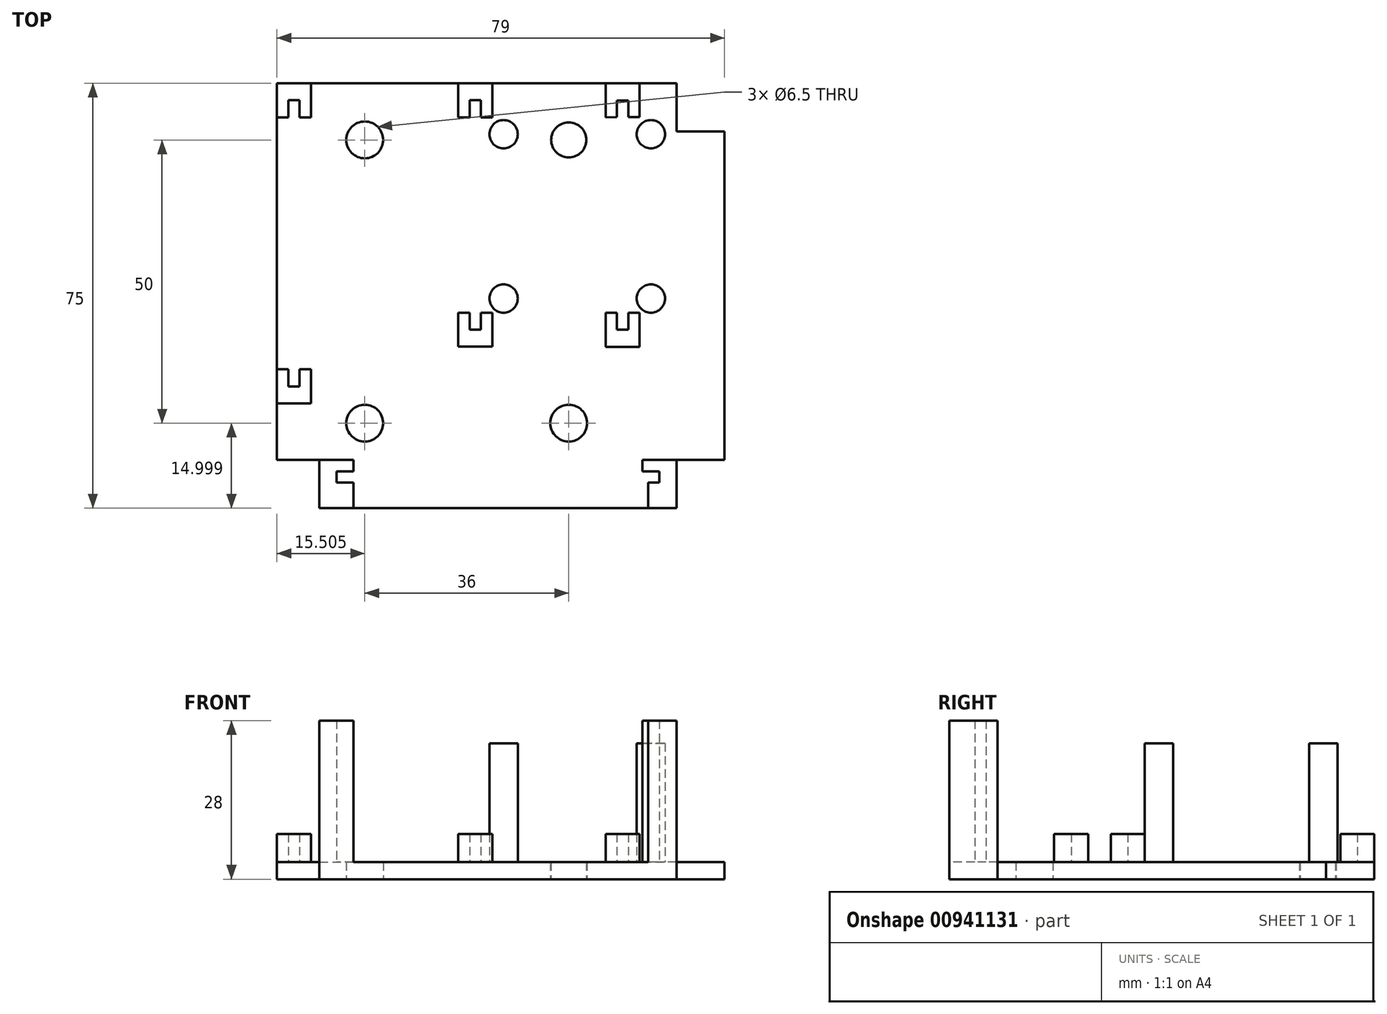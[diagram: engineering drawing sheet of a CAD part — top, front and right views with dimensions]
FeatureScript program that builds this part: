
annotation { "Feature Type Name" : "Feature", "Feature Type Description" : "" }
export const myFeature = defineFeature(function(context is Context, id is Id, definition is map)
    precondition{}
    {
        {
            var Q0;
            Q0=qCreatedBy(makeId("Top.planeOp"),FACE);
            var sketch = newSketch(context, id + "F0", { "sketchPlane" : qUnion([Q0])});
            skLineSegment(sketch, "E0", {"start": v(0, 50.14) * mm, "end": v(-25.4, 50.14) * mm});
            skLineSegment(sketch, "E1", {"start": v(-25.4, 50.14) * mm, "end": v(-25.4, -16.36) * mm});
            skLineSegment(sketch, "E2", {"start": v(-25.4, -16.36) * mm, "end": v(-17.9, -16.36) * mm});
            skLineSegment(sketch, "E3", {"start": v(-17.9, -16.36) * mm, "end": v(-17.9, -24.86) * mm});
            skLineSegment(sketch, "E4", {"start": v(-17.9, -24.86) * mm, "end": v(0, -24.86) * mm});
            skLineSegment(sketch, "E5", {"start": v(0, -24.86) * mm, "end": v(45.1, -24.86) * mm});
            skLineSegment(sketch, "E6", {"start": v(45.1, -24.86) * mm, "end": v(45.1, -16.36) * mm});
            skLineSegment(sketch, "E7", {"start": v(45.1, -16.36) * mm, "end": v(53.6, -16.36) * mm});
            skLineSegment(sketch, "E8", {"start": v(53.6, -16.36) * mm, "end": v(53.6, 41.64) * mm});
            skLineSegment(sketch, "E9", {"start": v(53.6, 41.64) * mm, "end": v(45.1, 41.64) * mm});
            skLineSegment(sketch, "E10", {"start": v(45.1, 41.64) * mm, "end": v(45.1, 50.14) * mm});
            skLineSegment(sketch, "E11", {"start": v(45.1, 50.14) * mm, "end": v(0, 50.14) * mm});
            skCircle(sketch, "E12", {"center": v(-9.9, 40.14) * mm, "radius": 3.25 * mm});
            skCircle(sketch, "E13", {"center": v(-9.9, -9.86) * mm, "radius": 3.25 * mm});
            skCircle(sketch, "E14", {"center": v(26.1, -9.86) * mm, "radius": 3.25 * mm});
            skCircle(sketch, "E15", {"center": v(26.1, 40.14) * mm, "radius": 3.1 * mm});
            skSolve(sketch);
        }
        {
            var Q0;
            Q0=makeQuery(id+"F0.imprint","IMPRINT",FACE,{"disambiguationData":[TD([[makeQuery(id+"F0.imprint","IMPRINT",EDGE,{"derivedFrom":sQuery(id+"F0.wireOp",EDGE,"E0")}),1.0]])]});
            extrude(context, id + "F1", {"entities" : qUnion([Q0]), "depth" : 3 * mm, "offsetDistance" : 25 * mm});
        }
        {
            var Q0;
            Q0=makeQuery(id+"F1.opExtrude","CAP_FACE",FACE,{"disambiguationData":[OSD([sQuery(id+"F0.wireOp",EDGE,"E0"),sQuery(id+"F0.wireOp",EDGE,"E1"),sQuery(id+"F0.wireOp",EDGE,"E2"),sQuery(id+"F0.wireOp",EDGE,"E3"),sQuery(id+"F0.wireOp",EDGE,"E4"),sQuery(id+"F0.wireOp",EDGE,"E5"),sQuery(id+"F0.wireOp",EDGE,"E6"),sQuery(id+"F0.wireOp",EDGE,"E7"),sQuery(id+"F0.wireOp",EDGE,"E8"),sQuery(id+"F0.wireOp",EDGE,"E9"),sQuery(id+"F0.wireOp",EDGE,"E10"),sQuery(id+"F0.wireOp",EDGE,"E11"),sQuery(id+"F0.wireOp",EDGE,"E12"),sQuery(id+"F0.wireOp",EDGE,"E13"),sQuery(id+"F0.wireOp",EDGE,"E14"),sQuery(id+"F0.wireOp",EDGE,"E15")])],"isStart":false});
            var sketch = newSketch(context, id + "F2", { "sketchPlane" : qUnion([Q0])});
            skLineSegment(sketch, "E16.bottom", {"start": v(-23.4, 47.14) * mm, "end": v(-21.4, 47.14) * mm});
            skLineSegment(sketch, "E16.top", {"start": v(-23.4, -3.36) * mm, "end": v(-21.4, -3.36) * mm});
            skLineSegment(sketch, "E16.left", {"start": v(-23.4, 47.14) * mm, "end": v(-23.4, -3.36) * mm});
            skLineSegment(sketch, "E16.right", {"start": v(-21.4, 47.14) * mm, "end": v(-21.4, -3.36) * mm});
            skLineSegment(sketch, "E17", {"start": v(-23.4, 44.14) * mm, "end": v(-25.4, 44.14) * mm});
            skLineSegment(sketch, "E18", {"start": v(-25.4, 44.14) * mm, "end": v(-25.4, 50.14) * mm});
            skLineSegment(sketch, "E19", {"start": v(-25.4, 50.14) * mm, "end": v(-19.4, 50.14) * mm});
            skLineSegment(sketch, "E20", {"start": v(-19.4, 50.14) * mm, "end": v(-19.4, 44.14) * mm});
            skLineSegment(sketch, "E21", {"start": v(-19.4, 44.14) * mm, "end": v(-21.4, 44.14) * mm});
            skLineSegment(sketch, "E22", {"start": v(-21.4, 44.14) * mm, "end": v(-21.4, 0) * mm});
            skLineSegment(sketch, "E23", {"start": v(-25.4, -0.36) * mm, "end": v(-25.4, -6.36) * mm});
            skLineSegment(sketch, "E24", {"start": v(-25.4, -6.36) * mm, "end": v(-19.4, -6.36) * mm});
            skLineSegment(sketch, "E25", {"start": v(-19.4, -6.36) * mm, "end": v(-19.4, -0.36) * mm});
            skLineSegment(sketch, "E26", {"start": v(-25.4, -0.36) * mm, "end": v(-23.4, -0.36) * mm});
            skLineSegment(sketch, "E27", {"start": v(-19.4, -0.36) * mm, "end": v(-21.4, -0.36) * mm});
            skLineSegment(sketch, "E28", {"start": v(6.6, 50.14) * mm, "end": v(6.6, 44.14) * mm});
            skLineSegment(sketch, "E29", {"start": v(6.6, 44.14) * mm, "end": v(8.6, 44.13) * mm});
            skLineSegment(sketch, "E30", {"start": v(8.6, 44.13) * mm, "end": v(8.6, 47.14) * mm});
            skLineSegment(sketch, "E31", {"start": v(8.6, 47.14) * mm, "end": v(10.6, 47.14) * mm});
            skLineSegment(sketch, "E32", {"start": v(10.6, 47.14) * mm, "end": v(10.6, 44.13) * mm});
            skLineSegment(sketch, "E33", {"start": v(10.6, 44.13) * mm, "end": v(12.6, 44.13) * mm});
            skLineSegment(sketch, "E34", {"start": v(12.6, 44.13) * mm, "end": v(12.6, 50.14) * mm});
            skLineSegment(sketch, "E35.top", {"start": v(8.6, 6.64) * mm, "end": v(10.6, 6.64) * mm});
            skLineSegment(sketch, "E35.left", {"start": v(8.6, 47.14) * mm, "end": v(8.6, 6.64) * mm});
            skLineSegment(sketch, "E35.right", {"start": v(10.6, 47.14) * mm, "end": v(10.6, 6.64) * mm});
            skLineSegment(sketch, "E36", {"start": v(8.6, 9.64) * mm, "end": v(6.6, 9.64) * mm});
            skLineSegment(sketch, "E37", {"start": v(6.6, 9.64) * mm, "end": v(6.6, 3.64) * mm});
            skLineSegment(sketch, "E38", {"start": v(6.6, 3.64) * mm, "end": v(12.6, 3.64) * mm});
            skLineSegment(sketch, "E39", {"start": v(12.6, 3.64) * mm, "end": v(12.6, 9.64) * mm});
            skLineSegment(sketch, "E40", {"start": v(12.6, 9.64) * mm, "end": v(10.6, 9.64) * mm});
            skLineSegment(sketch, "E41", {"start": v(32.6, 50.14) * mm, "end": v(32.6, 44.14) * mm});
            skLineSegment(sketch, "E42", {"start": v(32.6, 44.14) * mm, "end": v(34.6, 44.15) * mm});
            skLineSegment(sketch, "E43", {"start": v(34.6, 44.15) * mm, "end": v(34.6, 47.12) * mm});
            skLineSegment(sketch, "E44", {"start": v(34.6, 47.12) * mm, "end": v(36.6, 47.12) * mm});
            skLineSegment(sketch, "E45", {"start": v(36.6, 47.12) * mm, "end": v(36.6, 44.15) * mm});
            skLineSegment(sketch, "E46", {"start": v(36.6, 44.15) * mm, "end": v(38.6, 44.15) * mm});
            skLineSegment(sketch, "E47.top", {"start": v(34.6, 6.62) * mm, "end": v(36.6, 6.62) * mm});
            skLineSegment(sketch, "E47.left", {"start": v(34.6, 47.12) * mm, "end": v(34.6, 6.62) * mm});
            skLineSegment(sketch, "E47.right", {"start": v(36.6, 47.12) * mm, "end": v(36.6, 6.62) * mm});
            skLineSegment(sketch, "E48", {"start": v(34.6, 9.62) * mm, "end": v(32.6, 9.62) * mm});
            skLineSegment(sketch, "E49", {"start": v(32.6, 9.62) * mm, "end": v(32.6, 3.62) * mm});
            skLineSegment(sketch, "E50", {"start": v(32.6, 3.62) * mm, "end": v(38.6, 3.62) * mm});
            skLineSegment(sketch, "E51", {"start": v(38.6, 3.62) * mm, "end": v(38.6, 9.62) * mm});
            skLineSegment(sketch, "E52", {"start": v(38.6, 9.62) * mm, "end": v(36.6, 9.62) * mm});
            skLineSegment(sketch, "E53", {"start": v(38.6, 44.15) * mm, "end": v(38.6, 50.14) * mm});
            skLineSegment(sketch, "E54", {"start": v(45.1, -16.36) * mm, "end": v(39.1, -16.36) * mm});
            skLineSegment(sketch, "E55", {"start": v(39.1, -16.36) * mm, "end": v(39.1, -18.36) * mm});
            skLineSegment(sketch, "E56", {"start": v(39.1, -18.36) * mm, "end": v(42.1, -18.36) * mm});
            skLineSegment(sketch, "E57", {"start": v(42.1, -18.36) * mm, "end": v(42.1, -20.36) * mm});
            skLineSegment(sketch, "E58", {"start": v(42.1, -20.36) * mm, "end": v(40.1, -20.36) * mm});
            skLineSegment(sketch, "E59", {"start": v(40.1, -20.36) * mm, "end": v(40.1, -24.86) * mm});
            skLineSegment(sketch, "E60", {"start": v(-17.9, -16.36) * mm, "end": v(-11.9, -16.36) * mm});
            skLineSegment(sketch, "E61", {"start": v(-11.9, -16.36) * mm, "end": v(-11.9, -18.36) * mm});
            skLineSegment(sketch, "E62", {"start": v(-11.9, -18.36) * mm, "end": v(-14.9, -18.36) * mm});
            skLineSegment(sketch, "E63", {"start": v(-14.9, -18.36) * mm, "end": v(-14.9, -20.36) * mm});
            skLineSegment(sketch, "E64", {"start": v(-14.9, -20.36) * mm, "end": v(-11.9, -20.36) * mm});
            skLineSegment(sketch, "E65", {"start": v(-11.9, -20.36) * mm, "end": v(-11.9, -24.86) * mm});
            skLineSegment(sketch, "E66", {"start": v(-17.9, -16.36) * mm, "end": v(-17.9, -24.86) * mm});
            skLineSegment(sketch, "E67", {"start": v(-17.9, -24.86) * mm, "end": v(-11.9, -24.86) * mm});
            skLineSegment(sketch, "E68", {"start": v(40.1, -24.86) * mm, "end": v(45.1, -24.86) * mm});
            skLineSegment(sketch, "E69", {"start": v(45.1, -24.86) * mm, "end": v(45.1, -16.36) * mm});
            skCircle(sketch, "E70", {"center": v(14.6, 41.14) * mm, "radius": 2.5 * mm});
            skCircle(sketch, "E71", {"center": v(40.6, 41.14) * mm, "radius": 2.5 * mm});
            skCircle(sketch, "E72", {"center": v(40.6, 12.14) * mm, "radius": 2.5 * mm});
            skCircle(sketch, "E73", {"center": v(14.6, 12.14) * mm, "radius": 2.5 * mm});
            skSolve(sketch);
        }
        {
            var Q0;
            {var subQ2=sQuery(id+"F2.wireOp",EDGE,"E16.bottom");Q0=makeQuery(id+"F2.imprint","IMPRINT",FACE,{"disambiguationData":[TD([[makeQuery(id+"F2.imprint","IMPRINT",EDGE,{"derivedFrom":subQ2}),1.0]])]});}
            var Q1;
            {var subQ1=sQuery(id+"F2.wireOp",EDGE,"E28");Q1=makeQuery(id+"F2.imprint","IMPRINT",FACE,{"disambiguationData":[TD([[makeQuery(id+"F2.imprint","IMPRINT",EDGE,{"derivedFrom":subQ1}),1.0]])]});}
            var Q2;
            {var subQ2=sQuery(id+"F2.wireOp",EDGE,"E35.top");Q2=makeQuery(id+"F2.imprint","IMPRINT",FACE,{"disambiguationData":[TD([[makeQuery(id+"F2.imprint","IMPRINT",EDGE,{"derivedFrom":subQ2}),-1.0]])]});}
            var Q3;
            {var subQ1=sQuery(id+"F2.wireOp",EDGE,"E47.top");Q3=makeQuery(id+"F2.imprint","IMPRINT",FACE,{"disambiguationData":[TD([[makeQuery(id+"F2.imprint","IMPRINT",EDGE,{"derivedFrom":subQ1}),-1.0]])]});}
            var Q4;
            {var subQ1=sQuery(id+"F2.wireOp",EDGE,"E16.top");Q4=makeQuery(id+"F2.imprint","IMPRINT",FACE,{"disambiguationData":[TD([[makeQuery(id+"F2.imprint","IMPRINT",EDGE,{"derivedFrom":subQ1}),-1.0]])]});}
            var Q5;
            {var subQ1=sQuery(id+"F2.wireOp",EDGE,"E41");Q5=makeQuery(id+"F2.imprint","IMPRINT",FACE,{"disambiguationData":[TD([[makeQuery(id+"F2.imprint","IMPRINT",EDGE,{"derivedFrom":subQ1}),1.0]])]});}
            extrude(context, id + "F3", {"entities" : qUnion([Q0, Q1, Q2, Q3, Q4, Q5]), "operationType" : NewBodyOperationType.ADD, "depth" : 5 * mm, "offsetDistance" : 25 * mm});
        }
        {
            var Q0;
            Q0=makeQuery(id+"F2.imprint","IMPRINT",FACE,{"disambiguationData":[TD([[makeQuery(id+"F2.imprint","IMPRINT",EDGE,{"derivedFrom":sQuery(id+"F2.wireOp",EDGE,"E60")}),-1.0]])]});
            var Q1;
            Q1=makeQuery(id+"F2.imprint","IMPRINT",FACE,{"disambiguationData":[TD([[makeQuery(id+"F2.imprint","IMPRINT",EDGE,{"derivedFrom":sQuery(id+"F2.wireOp",EDGE,"E54")}),1.0]])]});
            extrude(context, id + "F4", {"entities" : qUnion([Q0, Q1]), "operationType" : NewBodyOperationType.ADD, "depth" : 25 * mm, "offsetDistance" : 25 * mm});
        }
        {
            var Q0;
            Q0=makeQuery(id+"F2.imprint","IMPRINT",FACE,{"disambiguationData":[TD([[makeQuery(id+"F2.imprint","IMPRINT",EDGE,{"derivedFrom":sQuery(id+"F2.wireOp",EDGE,"E70")}),1.0]])]});
            var Q1;
            Q1=makeQuery(id+"F2.imprint","IMPRINT",FACE,{"disambiguationData":[TD([[makeQuery(id+"F2.imprint","IMPRINT",EDGE,{"derivedFrom":sQuery(id+"F2.wireOp",EDGE,"E73")}),1.0]])]});
            var Q2;
            Q2=makeQuery(id+"F2.imprint","IMPRINT",FACE,{"disambiguationData":[TD([[makeQuery(id+"F2.imprint","IMPRINT",EDGE,{"derivedFrom":sQuery(id+"F2.wireOp",EDGE,"E72")}),1.0]])]});
            var Q3;
            Q3=makeQuery(id+"F2.imprint","IMPRINT",FACE,{"disambiguationData":[TD([[makeQuery(id+"F2.imprint","IMPRINT",EDGE,{"derivedFrom":sQuery(id+"F2.wireOp",EDGE,"E71")}),1.0]])]});
            extrude(context, id + "F5", {"entities" : qUnion([Q0, Q1, Q2, Q3]), "operationType" : NewBodyOperationType.ADD, "depth" : 21 * mm, "offsetDistance" : 25 * mm});
        }
    });
